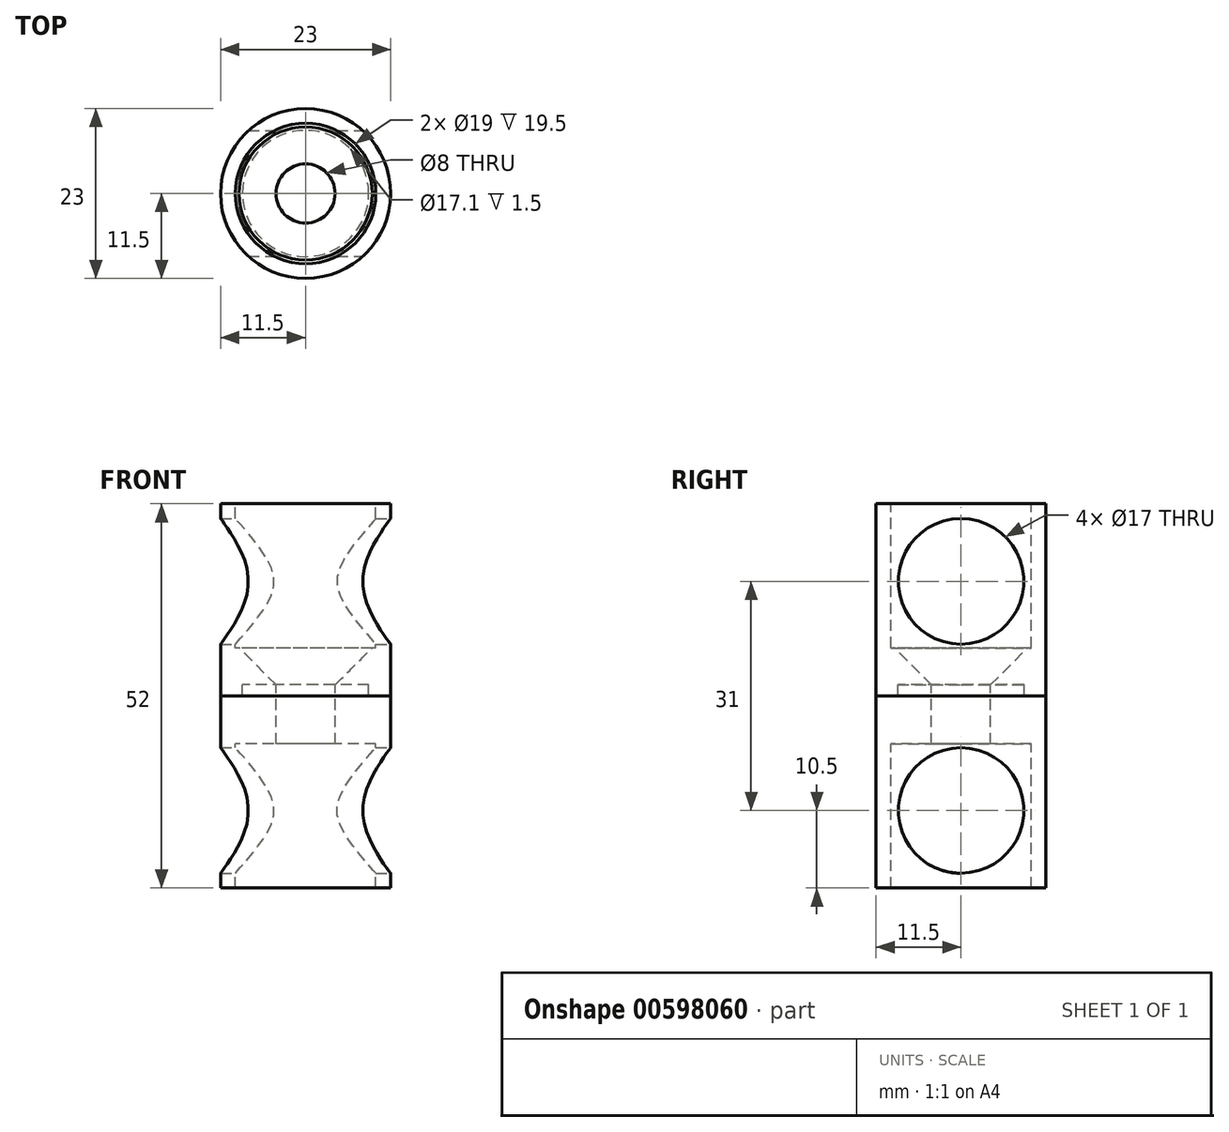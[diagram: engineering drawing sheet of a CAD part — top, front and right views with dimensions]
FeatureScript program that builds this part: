
annotation { "Feature Type Name" : "Feature", "Feature Type Description" : "" }
export const myFeature = defineFeature(function(context is Context, id is Id, definition is map)
    precondition{}
    {
        {
            var Q0;
            Q0=qCreatedBy(makeId("Front.planeOp"),FACE);
            var sketch = newSketch(context, id + "F0", { "sketchPlane" : qUnion([Q0])});
            skLineSegment(sketch, "E0", {"start": v(-9.5, 0) * mm, "end": v(-11.5, 0) * mm});
            skLineSegment(sketch, "E1", {"start": v(-11.5, 0) * mm, "end": v(-11.5, 52) * mm});
            skLineSegment(sketch, "E2", {"start": v(-11.5, 52) * mm, "end": v(-9.5, 52) * mm});
            skLineSegment(sketch, "E3", {"start": v(0, 32.5) * mm, "end": v(0, 0) * mm, "construction": true});
            skLineSegment(sketch, "E4", {"start": v(-9.5, 52) * mm, "end": v(-9.5, 32.5) * mm});
            skLineSegment(sketch, "E5", {"start": v(-9.5, 32.5) * mm, "end": v(-9, 32.5) * mm});
            skLineSegment(sketch, "E6", {"start": v(-9.5, 0) * mm, "end": v(-9.5, 19.5) * mm});
            skLineSegment(sketch, "E7", {"start": v(-9.5, 19.5) * mm, "end": v(-4, 19.5) * mm});
            skLineSegment(sketch, "E8", {"start": v(-9, 32.5) * mm, "end": v(-4, 27.5) * mm});
            skPoint(sketch, "E9", {"position": v(-9.5, 26) * mm});
            skLineSegment(sketch, "E10", {"start": v(-4, 27.5) * mm, "end": v(-4, 19.5) * mm});
            skPoint(sketch, "E11.orphan", {"position": v(0, 32.5) * mm});
            skLineSegment(sketch, "E12", {"start": v(-4, 27.5) * mm, "end": v(-8.55, 27.5) * mm});
            skLineSegment(sketch, "E13", {"start": v(-8.55, 27.5) * mm, "end": v(-8.55, 26) * mm});
            skLineSegment(sketch, "E14", {"start": v(-8.55, 26) * mm, "end": v(-11.5, 26) * mm});
            skLineSegment(sketch, "E15", {"start": v(-30.9, 41.5) * mm, "end": v(54.18, 41.5) * mm, "construction": true});
            skSolve(sketch);
        }
        {
            var Q0;
            {var subQ0=sQuery(id+"F0.wireOp",EDGE,"E2");Q0=makeQuery(id+"F0.imprint","IMPRINT",FACE,{"disambiguationData":[TD([[makeQuery(id+"F0.imprint","IMPRINT",EDGE,{"derivedFrom":subQ0}),-1.0]])]});}
            var Q1;
            Q1=sQuery(id+"F0.wireOp",EDGE,"E3");
            revolve(context, id + "F1", {"entities" : qUnion([Q0]), "axis" : qUnion([Q1]), "revolveType" : RevolveType.FULL});
        }
        {
            var Q0;
            {var subQ1=sQuery(id+"F0.wireOp",EDGE,"E0");Q0=makeQuery(id+"F0.imprint","IMPRINT",FACE,{"disambiguationData":[TD([[makeQuery(id+"F0.imprint","IMPRINT",EDGE,{"derivedFrom":subQ1}),-1.0]])]});}
            var Q1;
            Q1=sQuery(id+"F0.wireOp",EDGE,"E3");
            revolve(context, id + "F2", {"entities" : qUnion([Q0]), "axis" : qUnion([Q1]), "revolveType" : RevolveType.FULL});
        }
        {
            var Q0;
            Q0=qCreatedBy(makeId("Right.planeOp"),FACE);
            var sketch = newSketch(context, id + "F3", { "sketchPlane" : qUnion([Q0])});
            skCircle(sketch, "E16", {"center": v(0, 41.5) * mm, "radius": 8.5 * mm});
            skCircle(sketch, "E17", {"center": v(0, 10.5) * mm, "radius": 8.5 * mm});
            skLineSegment(sketch, "E18", {"start": v(0, 41.5) * mm, "end": v(0, 26) * mm, "construction": true});
            skLineSegment(sketch, "E19", {"start": v(0, 26) * mm, "end": v(0, 10.5) * mm, "construction": true});
            skSolve(sketch);
        }
        {
            var Q0;
            Q0 = qSketchRegion(id + "F3", true);
            extrude(context, id + "F4", {"entities" : qUnion([Q0]), "operationType" : NewBodyOperationType.REMOVE, "oppositeDirection" : true, "depth" : 54.2 * mm, "offsetDistance" : 25 * mm, "symmetric" : true});
        }
    });
